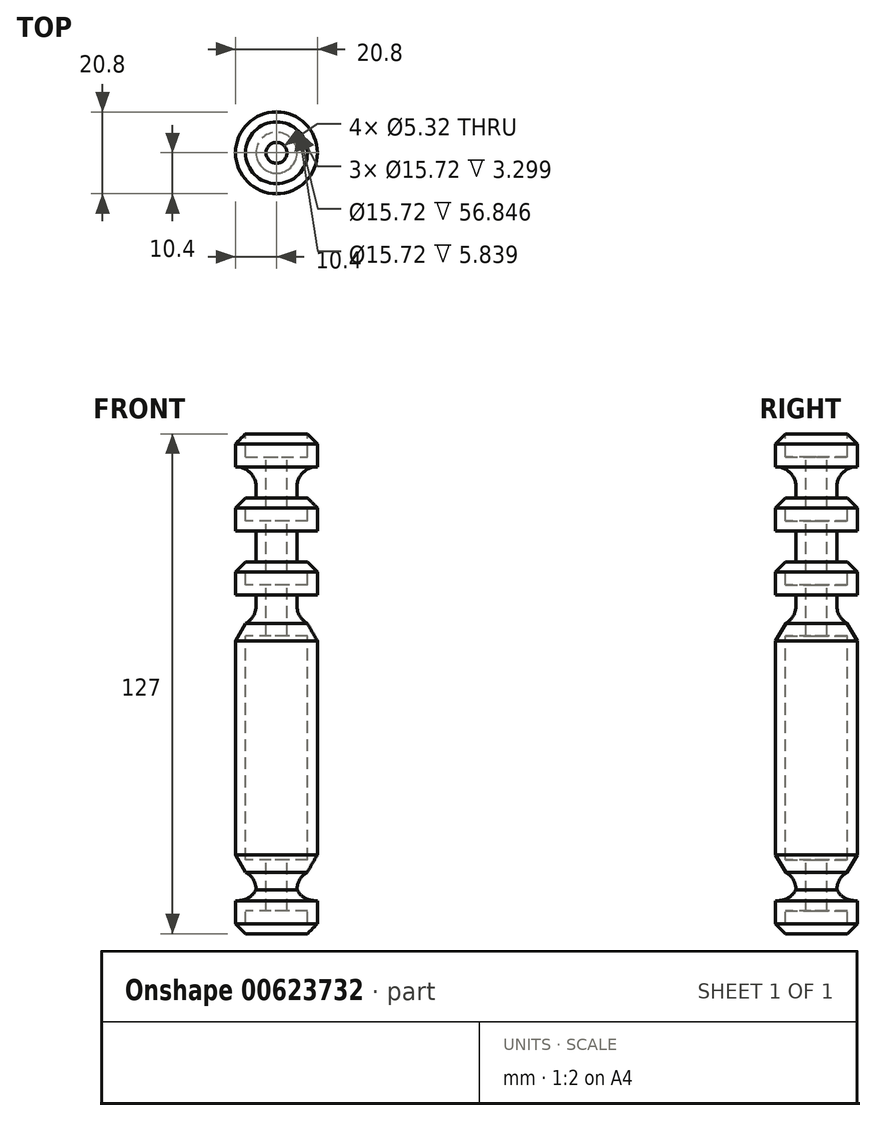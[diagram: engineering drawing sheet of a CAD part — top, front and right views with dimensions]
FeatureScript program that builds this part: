
annotation { "Feature Type Name" : "Feature", "Feature Type Description" : "" }
export const myFeature = defineFeature(function(context is Context, id is Id, definition is map)
    precondition{}
    {
        {
            var Q0;
            Q0=qCreatedBy(makeId("Front.planeOp"),FACE);
            var sketch = newSketch(context, id + "F0", { "sketchPlane" : qUnion([Q0])});
            skLineSegment(sketch, "E0.bottom", {"start": v(-10.4, 71.51) * mm, "end": v(0, 71.51) * mm});
            skLineSegment(sketch, "E0.top", {"start": v(-10.4, 63.13) * mm, "end": v(0, 63.13) * mm});
            skLineSegment(sketch, "E0.left", {"start": v(-10.4, 71.51) * mm, "end": v(-10.4, 63.13) * mm});
            skLineSegment(sketch, "E0.right", {"start": v(0, 71.51) * mm, "end": v(0, 63.13) * mm});
            skLineSegment(sketch, "E1.bottom", {"start": v(-5.2, 63.13) * mm, "end": v(0, 63.13) * mm});
            skLineSegment(sketch, "E1.top", {"start": v(-5.2, 55.25) * mm, "end": v(0, 55.25) * mm});
            skLineSegment(sketch, "E1.left", {"start": v(-5.2, 63.13) * mm, "end": v(-5.2, 55.25) * mm});
            skLineSegment(sketch, "E1.right", {"start": v(0, 63.13) * mm, "end": v(0, 55.25) * mm});
            skLineSegment(sketch, "E2.bottom", {"start": v(0, 55.25) * mm, "end": v(-10.4, 55.25) * mm});
            skLineSegment(sketch, "E2.top", {"start": v(0, 46.87) * mm, "end": v(-10.4, 46.87) * mm});
            skLineSegment(sketch, "E2.left", {"start": v(0, 55.25) * mm, "end": v(0, 46.87) * mm});
            skLineSegment(sketch, "E2.right", {"start": v(-10.4, 55.25) * mm, "end": v(-10.4, 46.87) * mm});
            skPoint(sketch, "E3.oppositeSnap0", {"position": v(0, 51.06) * mm});
            skLineSegment(sketch, "E3.bottom", {"start": v(-5.2, 46.87) * mm, "end": v(0, 46.87) * mm});
            skLineSegment(sketch, "E3.top", {"start": v(-5.2, 38.98) * mm, "end": v(0, 38.98) * mm});
            skLineSegment(sketch, "E3.left", {"start": v(-5.2, 46.87) * mm, "end": v(-5.2, 38.98) * mm});
            skLineSegment(sketch, "E3.right", {"start": v(0, 46.87) * mm, "end": v(0, 38.98) * mm});
            skLineSegment(sketch, "E4.bottom", {"start": v(0, 38.98) * mm, "end": v(-10.4, 38.98) * mm});
            skLineSegment(sketch, "E4.top", {"start": v(0, 30.6) * mm, "end": v(-10.4, 30.6) * mm});
            skLineSegment(sketch, "E4.left", {"start": v(0, 38.98) * mm, "end": v(0, 30.6) * mm});
            skLineSegment(sketch, "E4.right", {"start": v(-10.4, 38.98) * mm, "end": v(-10.4, 30.6) * mm});
            skPoint(sketch, "E5.oppositeSnap0", {"position": v(0, 34.79) * mm});
            skLineSegment(sketch, "E5.bottom", {"start": v(-5.2, 30.6) * mm, "end": v(0, 30.6) * mm});
            skLineSegment(sketch, "E5.top", {"start": v(-5.2, 22.7) * mm, "end": v(0, 22.7) * mm});
            skLineSegment(sketch, "E5.left", {"start": v(-5.2, 30.6) * mm, "end": v(-5.2, 22.7) * mm});
            skLineSegment(sketch, "E5.right", {"start": v(0, 30.6) * mm, "end": v(0, 22.7) * mm});
            skLineSegment(sketch, "E6.bottom", {"start": v(0, 22.7) * mm, "end": v(-10.4, 22.7) * mm});
            skLineSegment(sketch, "E6.top", {"start": v(0, -39.22) * mm, "end": v(-10.4, -39.22) * mm});
            skLineSegment(sketch, "E6.left", {"start": v(0, 22.7) * mm, "end": v(0, -39.22) * mm});
            skLineSegment(sketch, "E6.right", {"start": v(-10.4, 22.7) * mm, "end": v(-10.4, -39.22) * mm});
            skLineSegment(sketch, "E7.bottom", {"start": v(0, -39.22) * mm, "end": v(-5.2, -39.22) * mm});
            skLineSegment(sketch, "E7.top", {"start": v(0, -47.1) * mm, "end": v(-5.2, -47.1) * mm});
            skLineSegment(sketch, "E7.left", {"start": v(0, -39.22) * mm, "end": v(0, -47.1) * mm});
            skLineSegment(sketch, "E7.right", {"start": v(-5.2, -39.22) * mm, "end": v(-5.2, -47.1) * mm});
            skPoint(sketch, "E8.oppositeSnap0", {"position": v(-10.4, -8.25) * mm});
            skLineSegment(sketch, "E8.bottom", {"start": v(0, -47.1) * mm, "end": v(-10.4, -47.1) * mm});
            skLineSegment(sketch, "E8.top", {"start": v(0, -55.49) * mm, "end": v(-10.4, -55.49) * mm});
            skLineSegment(sketch, "E8.left", {"start": v(0, -47.1) * mm, "end": v(0, -55.49) * mm});
            skLineSegment(sketch, "E8.right", {"start": v(-10.4, -47.1) * mm, "end": v(-10.4, -55.49) * mm});
            skSolve(sketch);
        }
        {
            var Q0;
            Q0 = qSketchRegion(id + "F0", true);
            var Q1;
            Q1=sQuery(id+"F0.wireOp",EDGE,"E5.right");
            revolve(context, id + "F1", {"entities" : qUnion([Q0]), "axis" : qUnion([Q1]), "revolveType" : RevolveType.FULL});
        }
        {
            var Q0;
            Q0=makeQuery(id+"F1.opRevolve","SWEPT_FACE",FACE,{"disambiguationData":[OSD([sQuery(id+"F0.wireOp",EDGE,"E0.bottom")])]});
            shell(context, id + "F2", {"entities" : qUnion([Q0]), "thickness" : 2.54 * mm});
        }
        {
            var Q0;
            Q0=makeQuery(id+"F1.opRevolve","SWEPT_EDGE",EDGE,{"disambiguationData":[OSD([sQuery(id+"F0.wireOp",EDGE,"E0.bottom"),sQuery(id+"F0.wireOp",EDGE,"E0.left")])]});
            chamfer(context, id + "F3", {"entities" : qUnion([Q0]), "width" : 2.54 * mm, "tangentPropagation" : true});
        }
        {
            var Q0;
            Q0=makeQuery(id+"F1.opRevolve","SWEPT_EDGE",EDGE,{"disambiguationData":[OSD([sQuery(id+"F0.wireOp",EDGE,"E5.left"),sQuery(id+"F0.wireOp",EDGE,"E6.bottom")])]});
            fillet(context, id + "F4", {"entities" : qUnion([Q0]), "radius" : 5.08 * mm, "tangentPropagation" : true, "allowEdgeOverflow" : false});
        }
        {
            var Q0;
            Q0=makeQuery(id+"F1.opRevolve","SWEPT_EDGE",EDGE,{"disambiguationData":[OSD([sQuery(id+"F0.wireOp",EDGE,"E6.top"),sQuery(id+"F0.wireOp",EDGE,"E7.bottom"),sQuery(id+"F0.wireOp",EDGE,"E7.right")])]});
            fillet(context, id + "F5", {"entities" : qUnion([Q0]), "radius" : 5.08 * mm, "tangentPropagation" : true, "allowEdgeOverflow" : false});
        }
        {
            var Q0;
            Q0=makeQuery(id+"F1.opRevolve","SWEPT_EDGE",EDGE,{"disambiguationData":[OSD([sQuery(id+"F0.wireOp",EDGE,"E8.top"),sQuery(id+"F0.wireOp",EDGE,"E8.right")])]});
            chamfer(context, id + "F6", {"entities" : qUnion([Q0]), "width" : 2.54 * mm, "tangentPropagation" : true});
        }
        {
            var Q0;
            Q0=makeQuery(id+"F1.opRevolve","SWEPT_EDGE",EDGE,{"disambiguationData":[OSD([sQuery(id+"F0.wireOp",EDGE,"E2.bottom"),sQuery(id+"F0.wireOp",EDGE,"E2.right")])]});
            chamfer(context, id + "F7", {"entities" : qUnion([Q0]), "width" : 2.54 * mm, "tangentPropagation" : true});
        }
        {
            var Q0;
            Q0=makeQuery(id+"F1.opRevolve","SWEPT_EDGE",EDGE,{"disambiguationData":[OSD([sQuery(id+"F0.wireOp",EDGE,"E4.bottom"),sQuery(id+"F0.wireOp",EDGE,"E4.right")])]});
            chamfer(context, id + "F8", {"entities" : qUnion([Q0]), "width" : 2.54 * mm, "tangentPropagation" : true});
        }
        {
            var Q0;
            Q0=makeQuery(id+"F1.opRevolve","SWEPT_EDGE",EDGE,{"disambiguationData":[OSD([sQuery(id+"F0.wireOp",EDGE,"E0.top"),sQuery(id+"F0.wireOp",EDGE,"E1.bottom"),sQuery(id+"F0.wireOp",EDGE,"E1.left")])]});
            var Q1;
            Q1=makeQuery(id+"F1.opRevolve","SWEPT_EDGE",EDGE,{"disambiguationData":[OSD([sQuery(id+"F0.wireOp",EDGE,"E7.right"),sQuery(id+"F0.wireOp",EDGE,"E8.bottom")])]});
            fillet(context, id + "F9", {"entities" : qUnion([Q0, Q1]), "radius" : 5.08 * mm, "tangentPropagation" : true, "allowEdgeOverflow" : false});
        }
        {
            var Q0;
            Q0=makeQuery(id+"F1.opRevolve","SWEPT_EDGE",EDGE,{"disambiguationData":[OSD([sQuery(id+"F0.wireOp",EDGE,"E6.top"),sQuery(id+"F0.wireOp",EDGE,"E6.right")])]});
            var Q1;
            Q1=makeQuery(id+"F1.opRevolve","SWEPT_EDGE",EDGE,{"disambiguationData":[OSD([sQuery(id+"F0.wireOp",EDGE,"E6.bottom"),sQuery(id+"F0.wireOp",EDGE,"E6.right")])]});
            chamfer(context, id + "F10", {"entities" : qUnion([Q0, Q1]), "width" : 5.08 * mm, "tangentPropagation" : true});
        }
    });
